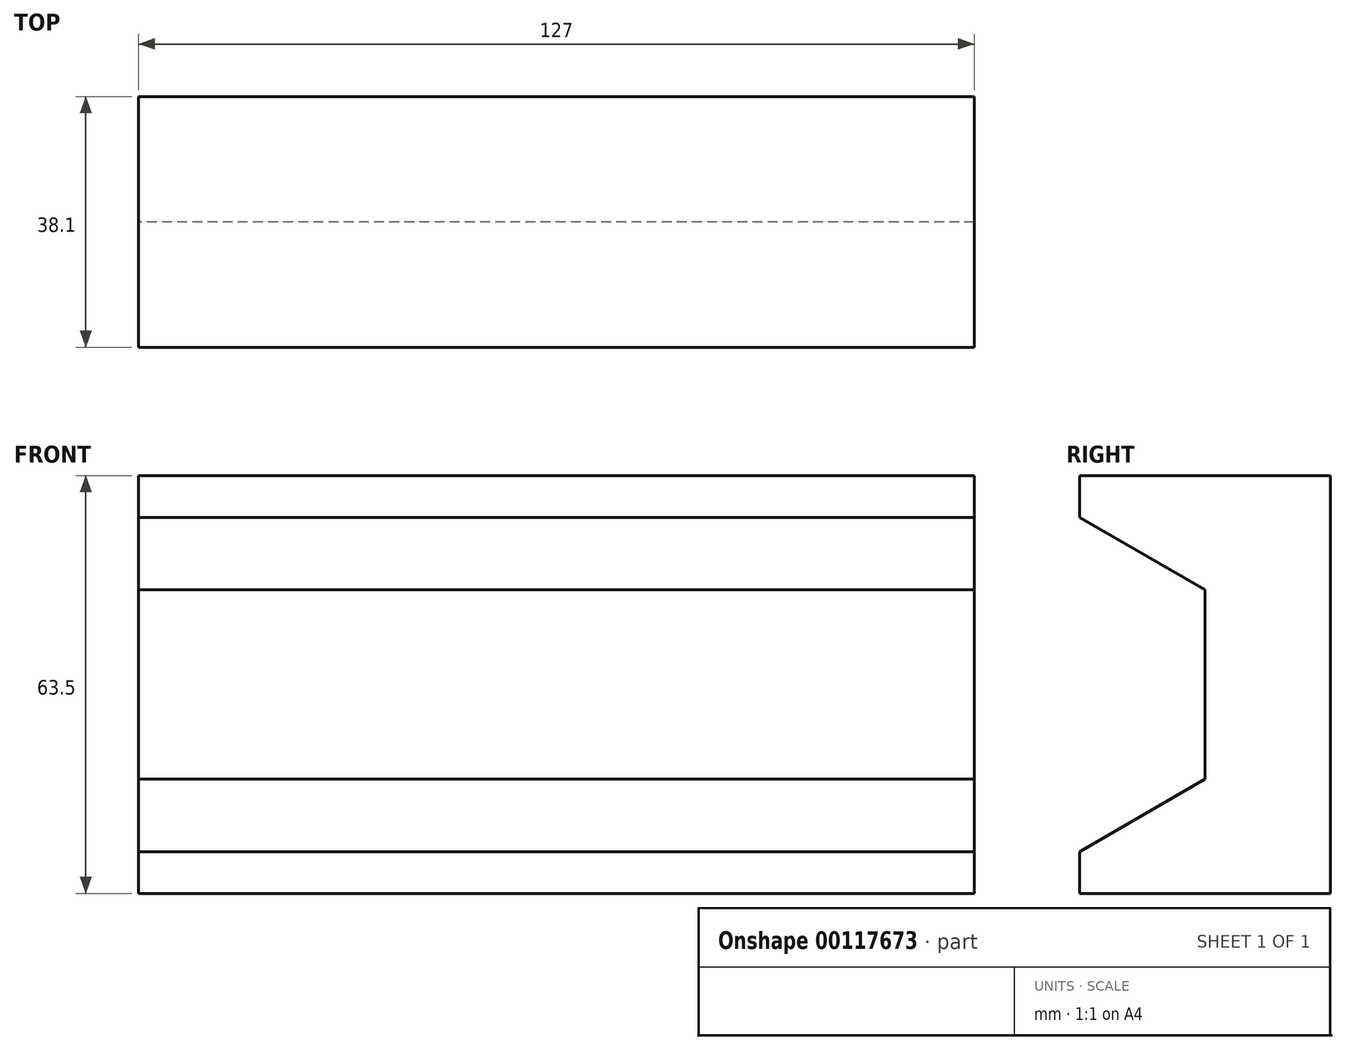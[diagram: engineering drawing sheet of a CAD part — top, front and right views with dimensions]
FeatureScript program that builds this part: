
annotation { "Feature Type Name" : "Feature", "Feature Type Description" : "" }
export const myFeature = defineFeature(function(context is Context, id is Id, definition is map)
    precondition{}
    {
        {
            var Q0;
            Q0=qCreatedBy(makeId("Right.planeOp"),FACE);
            var sketch = newSketch(context, id + "F0", { "sketchPlane" : qUnion([Q0])});
            skLineSegment(sketch, "E0.bottom", {"start": v(0, 0) * mm, "end": v(-38.1, 0) * mm});
            skLineSegment(sketch, "E0.top", {"start": v(0, 63.5) * mm, "end": v(-38.1, 63.5) * mm});
            skLineSegment(sketch, "E0.left", {"start": v(0, 0) * mm, "end": v(0, 63.5) * mm});
            skLineSegment(sketch, "E0.right", {"start": v(-38.1, 0) * mm, "end": v(-38.1, 6.35) * mm});
            skLineSegment(sketch, "E1", {"start": v(-38.1, 63.5) * mm, "end": v(-38.1, 57.15) * mm});
            skLineSegment(sketch, "E2", {"start": v(-38.1, 63.5) * mm, "end": v(-19.05, 63.5) * mm});
            skLineSegment(sketch, "E3", {"start": v(-38.1, 0) * mm, "end": v(-19.05, 0) * mm});
            skLineSegment(sketch, "E4", {"start": v(-19.05, 17.35) * mm, "end": v(-19.05, 46.15) * mm});
            skLineSegment(sketch, "E5", {"start": v(-38.1, 57.15) * mm, "end": v(-19.05, 46.15) * mm});
            skLineSegment(sketch, "E6", {"start": v(-38.1, 6.35) * mm, "end": v(-19.05, 17.35) * mm});
            skLineSegment(sketch, "E7.trimOffspring", {"start": v(-38.1, 57.15) * mm, "end": v(-38.1, 63.5) * mm});
            skSolve(sketch);
        }
        {
            var Q0;
            Q0=makeQuery(id+"F0.imprint","IMPRINT",FACE,{"disambiguationData":[TD([[makeQuery(id+"F0.imprint","IMPRINT",EDGE,{"derivedFrom":sQuery(id+"F0.wireOp",EDGE,"E0.bottom")}),-1.0]])]});
            extrude(context, id + "F1", {"entities" : qUnion([Q0]), "depth" : 127 * mm});
        }
    });
